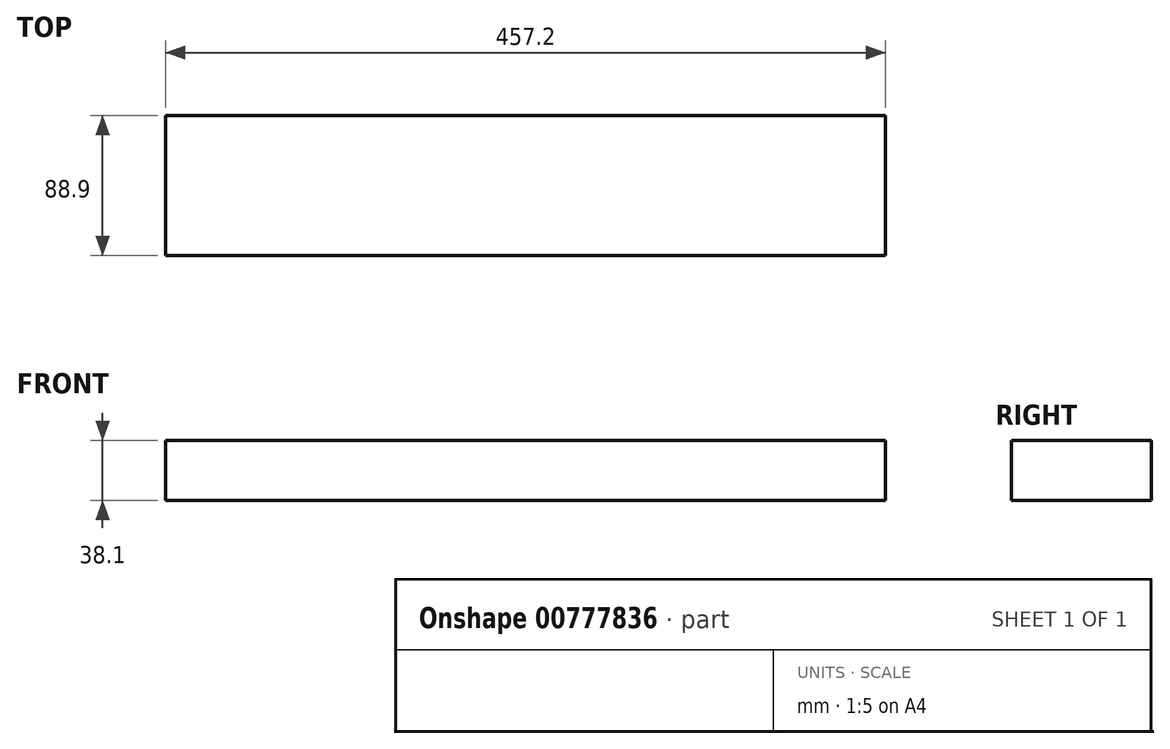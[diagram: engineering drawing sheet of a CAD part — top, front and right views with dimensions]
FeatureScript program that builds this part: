
annotation { "Feature Type Name" : "Feature", "Feature Type Description" : "" }
export const myFeature = defineFeature(function(context is Context, id is Id, definition is map)
    precondition{}
    {
        {
            var Q0;
            Q0=qCreatedBy(makeId("Right.planeOp"),FACE);
            var sketch = newSketch(context, id + "F0", { "sketchPlane" : qUnion([Q0])});
            skLineSegment(sketch, "E0.bottom", {"start": v(44.45, -19.05) * mm, "end": v(-44.45, -19.05) * mm});
            skLineSegment(sketch, "E0.top", {"start": v(44.45, 19.05) * mm, "end": v(-44.45, 19.05) * mm});
            skLineSegment(sketch, "E0.left", {"start": v(44.45, -19.05) * mm, "end": v(44.45, 19.05) * mm});
            skLineSegment(sketch, "E0.right", {"start": v(-44.45, -19.05) * mm, "end": v(-44.45, 19.05) * mm});
            skPoint(sketch, "E0.middle", {"position": v(0, 0) * mm});
            skSolve(sketch);
        }
        {
            var Q0;
            Q0 = qSketchRegion(id + "F0", true);
            extrude(context, id + "F1", {"entities" : qUnion([Q0]), "endBound" : BoundingType.SYMMETRIC, "depth" : 457.2 * mm, "offsetDistance" : 25.4 * mm});
        }
    });
